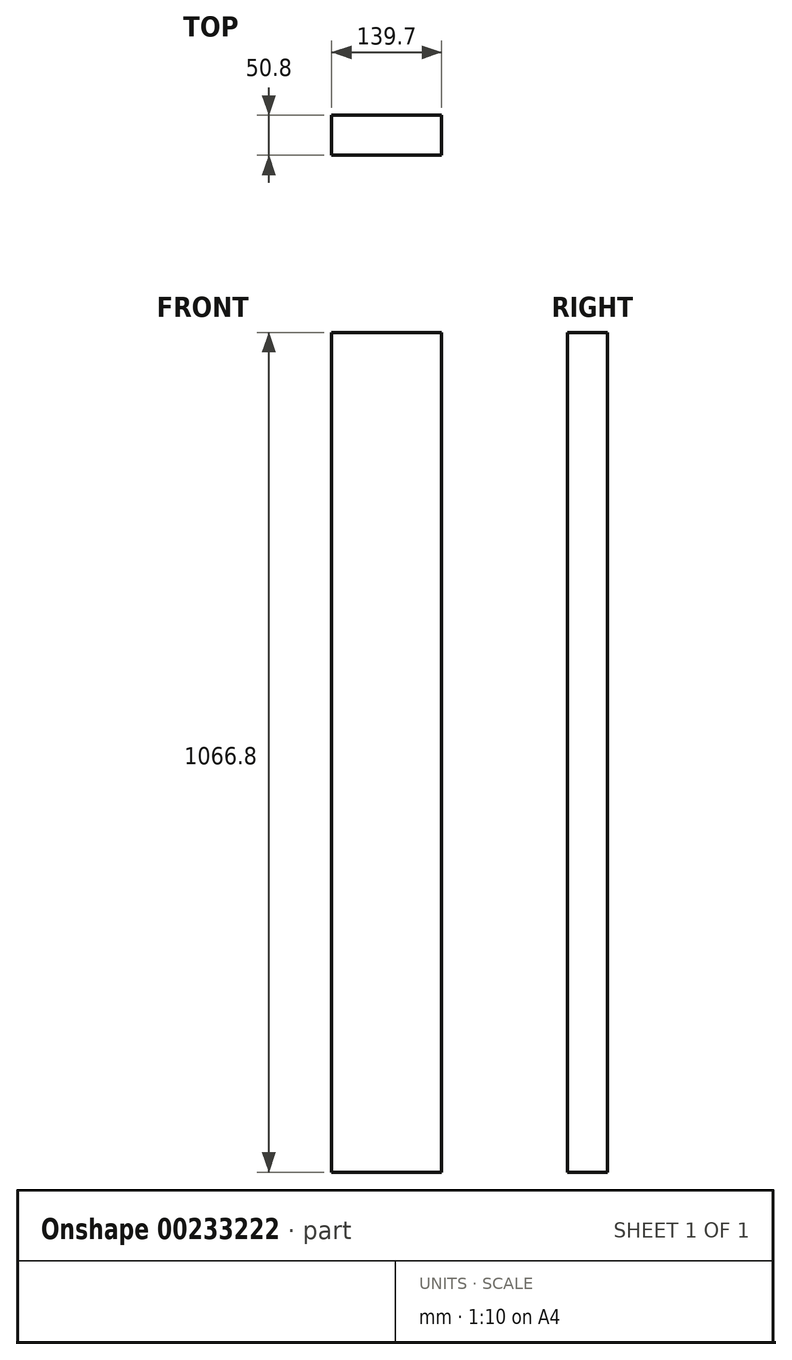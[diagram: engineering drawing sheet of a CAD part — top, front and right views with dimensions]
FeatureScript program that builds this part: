
annotation { "Feature Type Name" : "Feature", "Feature Type Description" : "" }
export const myFeature = defineFeature(function(context is Context, id is Id, definition is map)
    precondition{}
    {
        {
            var Q0;
            Q0=qCreatedBy(makeId("Front.planeOp"),FACE);
            var sketch = newSketch(context, id + "F0", { "sketchPlane" : qUnion([Q0])});
            skLineSegment(sketch, "E0.bottom", {"start": v(-159.6, 524.85) * mm, "end": v(-19.9, 524.85) * mm});
            skLineSegment(sketch, "E0.top", {"start": v(-159.6, -541.95) * mm, "end": v(-19.9, -541.95) * mm});
            skLineSegment(sketch, "E0.left", {"start": v(-159.6, 524.85) * mm, "end": v(-159.6, -541.95) * mm});
            skLineSegment(sketch, "E0.right", {"start": v(-19.9, 524.85) * mm, "end": v(-19.9, -541.95) * mm});
            skSolve(sketch);
        }
        {
            var Q0;
            Q0 = qSketchRegion(id + "F0", true);
            extrude(context, id + "F1", {"entities" : qUnion([Q0]), "depth" : 50.8 * mm});
        }
    });
